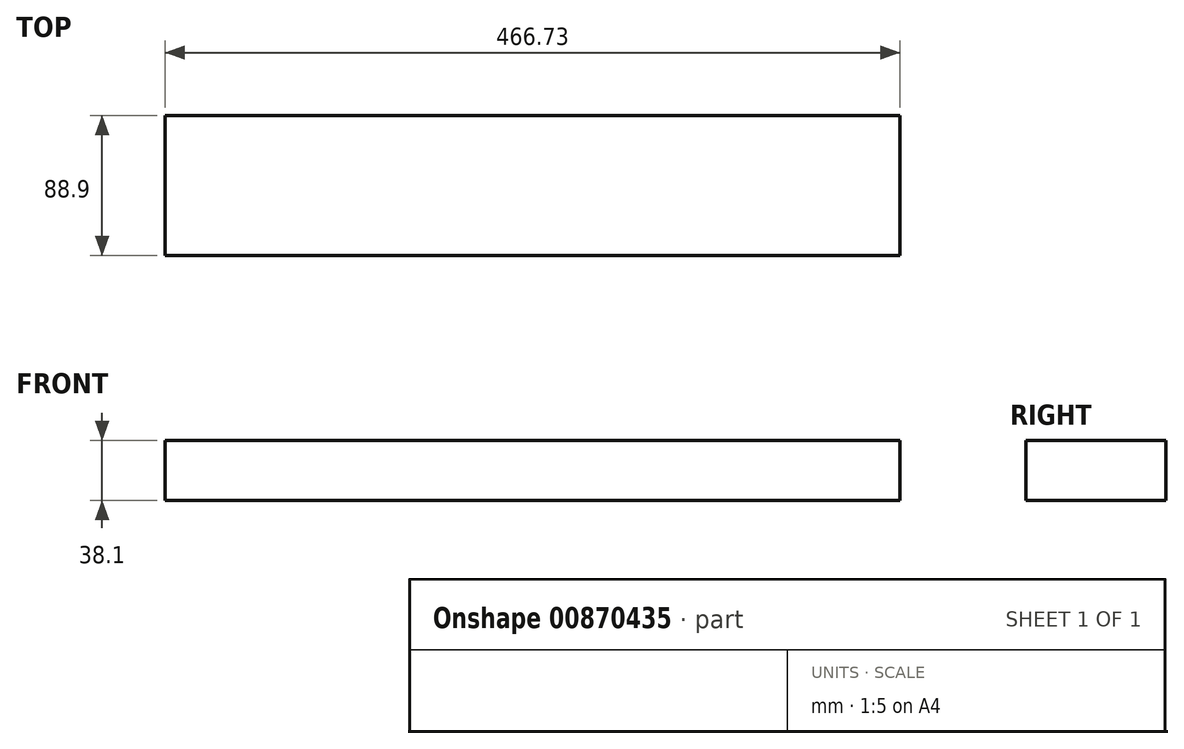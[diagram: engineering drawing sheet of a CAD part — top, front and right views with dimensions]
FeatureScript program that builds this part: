
annotation { "Feature Type Name" : "Feature", "Feature Type Description" : "" }
export const myFeature = defineFeature(function(context is Context, id is Id, definition is map)
    precondition{}
    {
        {
            var Q0;
            Q0=qCreatedBy(makeId("Right.planeOp"),FACE);
            var sketch = newSketch(context, id + "F0", { "sketchPlane" : qUnion([Q0])});
            skLineSegment(sketch, "E0.bottom", {"start": v(46.26, 19.05) * mm, "end": v(-42.64, 19.05) * mm});
            skLineSegment(sketch, "E0.top", {"start": v(46.26, -19.05) * mm, "end": v(-42.64, -19.05) * mm});
            skLineSegment(sketch, "E0.left", {"start": v(46.26, 19.05) * mm, "end": v(46.26, -19.05) * mm});
            skLineSegment(sketch, "E0.right", {"start": v(-42.64, 19.05) * mm, "end": v(-42.64, -19.05) * mm});
            skPoint(sketch, "E0.middle", {"position": v(1.8, 0) * mm});
            skSolve(sketch);
        }
        {
            var Q0;
            Q0=makeQuery(id+"F0.imprint","IMPRINT",FACE,{"disambiguationData":[TD([[makeQuery(id+"F0.imprint","IMPRINT",EDGE,{"derivedFrom":sQuery(id+"F0.wireOp",EDGE,"E0.bottom")}),1.0]])]});
            extrude(context, id + "F1", {"entities" : qUnion([Q0]), "depth" : 466.72 * mm, "offsetDistance" : 25.4 * mm});
        }
    });
